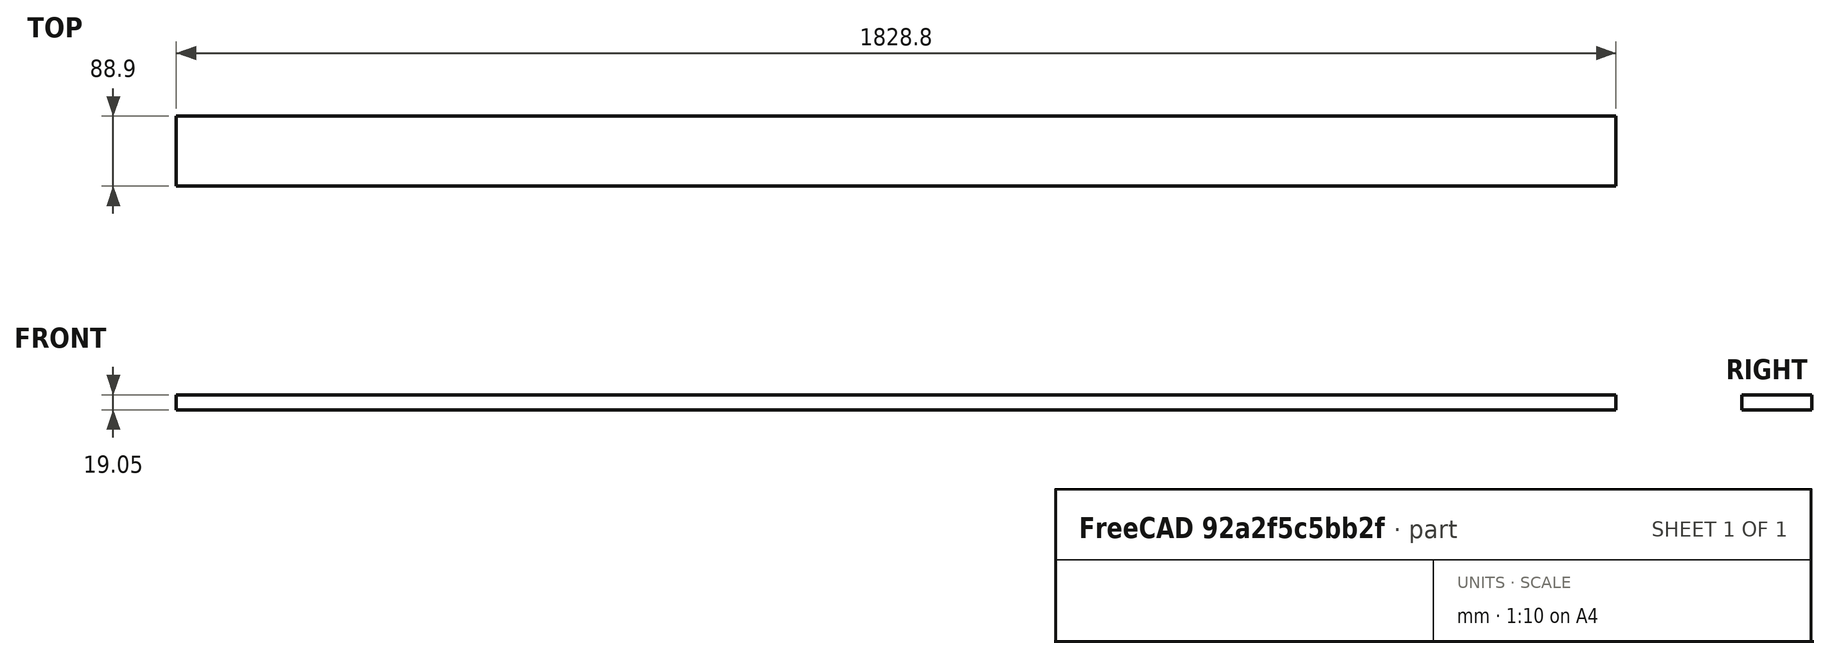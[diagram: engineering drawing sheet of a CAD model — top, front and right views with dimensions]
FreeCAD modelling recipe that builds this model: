
FCSTD DOCUMENT  (FreeCAD 0.21R33771 (Git))
Label: 1x4x6
License: All rights reserved
LicenseURL: http://en.wikipedia.org/wiki/All_rights_reserved
objects: Spreadsheet::Sheet×1, Sketcher::SketchObject×1, PartDesign::Pad×1, PartDesign::Body×1
note: 4 computed .brp shape members not serialized (recipe doc carries the construction recipe); baked Part::Feature solids carry a one-line shape summary decoded from their .brp

FEATURE [Spreadsheet::Sheet] Spreadsheet  label="var"
  cells = A2='varname; A3='len; B3(len)==25.4 * 72; A4='thk; B4(thk)==25.4 * 0.75; A5='wid; B5(wid)==25.4 * 3.5
FEATURE [Sketcher::SketchObject] Sketch
  FullyConstrained = true
  MapMode = 5
  Support = -> [XY_Plane]
  expr: Constraints[10] = Spreadsheet.wid
  expr: Constraints[9] = Spreadsheet.len
  sketch-geometry (4):
    g0: LineSegment StartX=-914.4 StartY=44.45 StartZ=0 EndX=914.4 EndY=44.45 EndZ=0
    g1: LineSegment StartX=914.4 StartY=44.45 StartZ=0 EndX=914.4 EndY=-44.45 EndZ=0
    g2: LineSegment StartX=914.4 StartY=-44.45 StartZ=0 EndX=-914.4 EndY=-44.45 EndZ=0
    g3: LineSegment StartX=-914.4 StartY=-44.45 StartZ=0 EndX=-914.4 EndY=44.45 EndZ=0
  constraints (11):
    c: Coincident(g0,g1)
    c: Coincident(g1,g2)
    c: Coincident(g2,g3)
    c: Coincident(g3,g0)
    c: Horizontal(g0)
    c: Horizontal(g2)
    c: Vertical(g1)
    c: Vertical(g3)
    c: Symmetric(g0,g2,g-1)
    c: Distance(g0,g0) = 1828.8
    c: Distance(g0,g2) = 88.9
FEATURE [PartDesign::Pad] Pad
  Direction = (0,0,1)
  Length = 19.05
  Length2 = 10
  Profile = -> Sketch
  ReferenceAxis = -> Sketch [N_Axis]
  Type = 0
  expr: Length = Spreadsheet.thk
FEATURE [PartDesign::Body] Body  label="body"
  Group = -> [Sketch,Pad]
  Origin = -> Origin
  Tip = -> Pad
